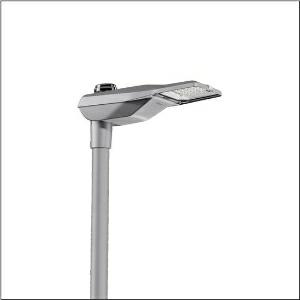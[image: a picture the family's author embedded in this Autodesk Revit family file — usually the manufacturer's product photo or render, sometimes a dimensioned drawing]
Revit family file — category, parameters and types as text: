
# Revit family: streetlight_sl_21_micro___st1_0a_5xe5d67n08db_977e
name_source: partatom
category: Lighting Fixtures
units: mm (PartAtom-declared; Revit-internal decimal feet)

## family parameters
Cut with Voids When Loaded = No
Host = Face
Light Source = No
Part Type = Normal
Room Calculation Point = No
Round Connector Dimension = Use Diameter
Shared = No

## types (1)
- --- (1 x LED, 4580 lm, 39.1 W, 2700K)
    Apparent Load = 39 VA
    CIE Flux Codes = 37 72 97 100 100
    Color Rendering = 70
    Color Temperature = 2700K
    Default Elevation = 1800 mm
    Description = Streetlight SL 21 micro, mast luminaire, primary light control with lens, of PMMA, primary optical cover: cover, of toughened safety glass, transparent, light distribution: ST1.0a, light emission: direct distribution, primary light characteristic: asymmetric, installation type: post-top, LED, 3G 1.5mm², High Power LED, rated luminous flux: 4.580lm, luminous efficacy: 117lm/W, light colour: 727, colour temperature: 2700K, control gear: NEMA (7pin), control: overheat protection, pre-setting: linear dimming characteristic, constant luminous flux control, time-dependent luminous flux control, flexible luminous flux parameterisation, mains connection: 230..240V, AC, 50/60Hz, connection cable pre-assembled, cable length: 6,5m, wiring characteristics: H07RN-F, start of lifetime: 39W, end of service life: 41W, reduction: 18W, luminaire housing, of diecast aluminium (EN AC-44300), powder-coated, Siteco® metallic grey (DB 702S), corrosivity category C5 mid according to DIN EN ISO 12944, multi-level sealing system, sealing non-destructively replaceable, inclination adjustable: 0°, 5°, 10°, 15°, length: 528mm, width: 235mm, height: 110mm, spigot size: 76/60mm (post-top), mounting height: 4..8m, protection rating (complete): IP66, insulation class (complete): insulation class I (protective earthing), certification: CE, ENEC, ENEC+, VDE, impact resistance: IK10, permissible operating ambient temperature for outdoor applications: -40..+50°C, standard-compliant lighting for roads and squares, packaging unit: 1 piece

Light Distribution: ST1.0a
    Height = 110 mm
    Lamp = 1 x LED
    Lamp Light Flux = 4580 lm
    Lamp Power = 39.1 W
    Lamp count = 1
    Length = 528 mm
    Luminous efficacy = 117 lm/W
    Manufacturer = Siteco
    ModVariant = No
    Model = 5XE5D67N08DB
    Number of Poles = 1
    OnlyDefault = Yes
    Power Factor = 1
    Product Name = Streetlight SL 21 micro | ST1.0a
    Product group = mast luminaire | pylon top
    ProductGroupID = 6100
    Protection Class = Protection class I
    Protection Degree = IP 66
    RLX_Detail_Level = 1
    RLX_Emergency_Light_Flux = 0 lm
    RLX_Emergency_Type = 0
    RLX_Emergency_Type_DB = No
    RlxData = <blob elided: 99001 chars, md5=fa862032>
    Socket = socket
    Standby Power = 0 W
    System Light Flux = 4580 lm
    System Power = 39 W
    Type Comments = factory setting: luminous flux: 100 % | dim-lin: 254 | 765 mA
    Type Image = l_1294375.jpg
    URL = http://relux.com
    VarID = @adj_157879
    Voltage = 0 V
    Weight = 0.00 kg
    Width = 235 mm

## geometry (parser evidence)
native form markers: Blend x4, Sweep x10
no freeform markers — native parametric forms only
